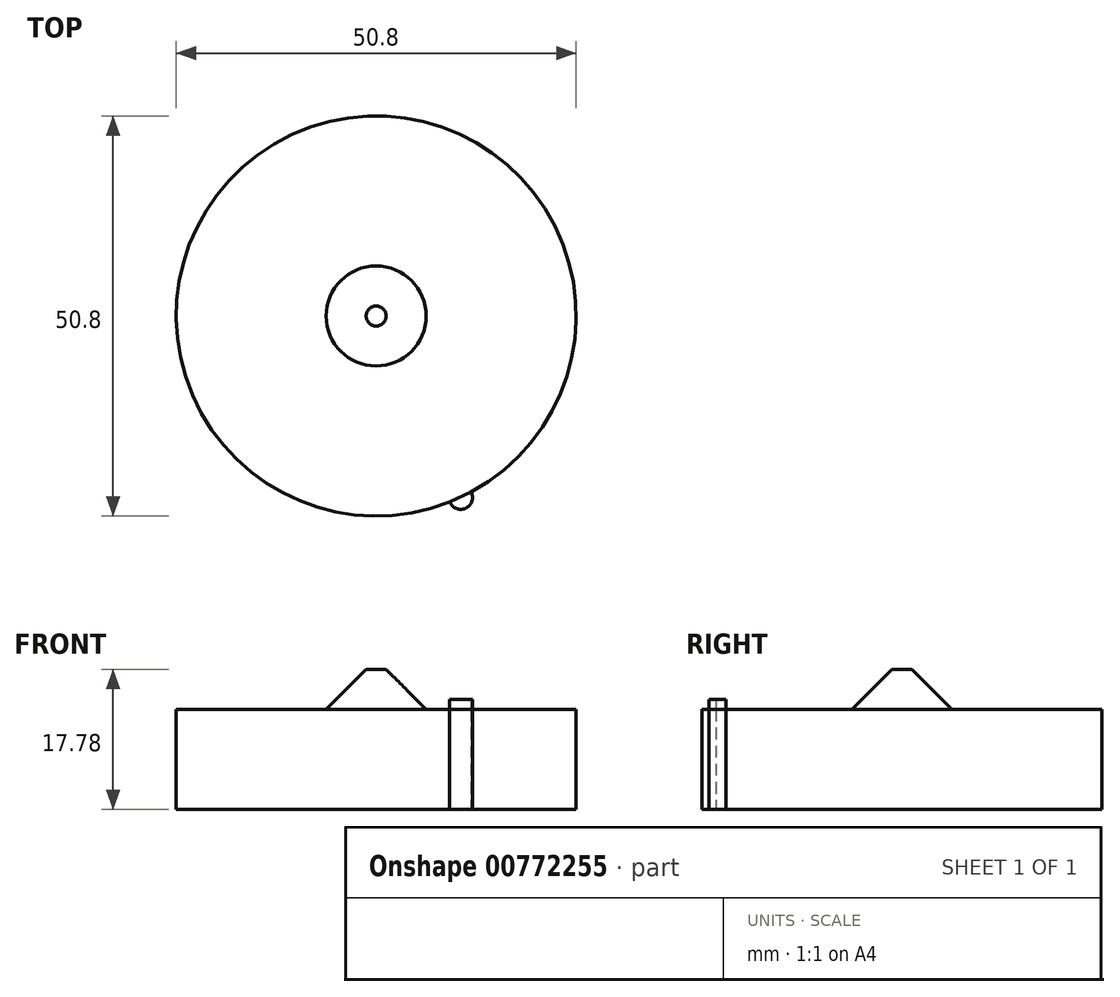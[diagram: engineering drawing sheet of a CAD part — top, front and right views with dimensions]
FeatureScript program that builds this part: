
annotation { "Feature Type Name" : "Feature", "Feature Type Description" : "" }
export const myFeature = defineFeature(function(context is Context, id is Id, definition is map)
    precondition{}
    {
        {
            var Q0;
            Q0=qCreatedBy(makeId("Top.planeOp"),FACE);
            var sketch = newSketch(context, id + "F0", { "sketchPlane" : qUnion([Q0])});
            skCircle(sketch, "E0", {"center": v(0, 0) * mm, "radius": 25.4 * mm});
            skCircle(sketch, "E1", {"center": v(0, 0) * mm, "radius": 6.35 * mm});
            skCircle(sketch, "E2", {"center": v(10.72, -23.02) * mm, "radius": 1.5 * mm});
            skSolve(sketch);
        }
        {
            var Q0;
            Q0 = qSketchRegion(id + "F0", true);
            extrude(context, id + "F1", {"entities" : qUnion([Q0]), "depth" : 12.7 * mm, "offsetDistance" : 25.4 * mm});
        }
        {
            var Q0;
            Q0=makeQuery(id+"F0.imprint","IMPRINT",FACE,{"disambiguationData":[TD([[makeQuery(id+"F0.imprint","IMPRINT",EDGE,{"derivedFrom":sQuery(id+"F0.wireOp",EDGE,"E1")}),1.0]])]});
            extrude(context, id + "F2", {"entities" : qUnion([Q0]), "operationType" : NewBodyOperationType.ADD, "depth" : 17.78 * mm, "offsetDistance" : 25.4 * mm});
        }
        {
            var Q0;
            Q0=makeQuery(id+"F2.opExtrude","CAP_EDGE",EDGE,{"disambiguationData":[OSD([sQuery(id+"F0.wireOp",EDGE,"E1")])],"isStart":false});
            chamfer(context, id + "F3", {"entities" : qUnion([Q0]), "width" : 5.08 * mm, "tangentPropagation" : true});
        }
        {
            var Q0;
            Q0=makeQuery(id+"F1.opExtrude","CAP_FACE",FACE,{"disambiguationData":[OSD([sQuery(id+"F0.wireOp",EDGE,"E0"),sQuery(id+"F0.wireOp",EDGE,"E1"),sQuery(id+"F0.wireOp",EDGE,"E2")])],"isStart":false});
            var sketch = newSketch(context, id + "F4", { "sketchPlane" : qUnion([Q0])});
            skArc(sketch, "E3", {"start": v(9.34, -23.62) * mm, "mid": v(11.37, -24.41) * mm, "end": v(12.07, -22.35) * mm});
            skLineSegment(sketch, "E4", {"start": v(12.07, -22.35) * mm, "end": v(9.34, -23.62) * mm});
            skSolve(sketch);
        }
        {
            var Q0;
            Q0 = qSketchRegion(id + "F4", true);
            extrude(context, id + "F5", {"entities" : qUnion([Q0]), "operationType" : NewBodyOperationType.ADD, "depth" : 1.27 * mm, "offsetDistance" : 25.4 * mm});
        }
    });
